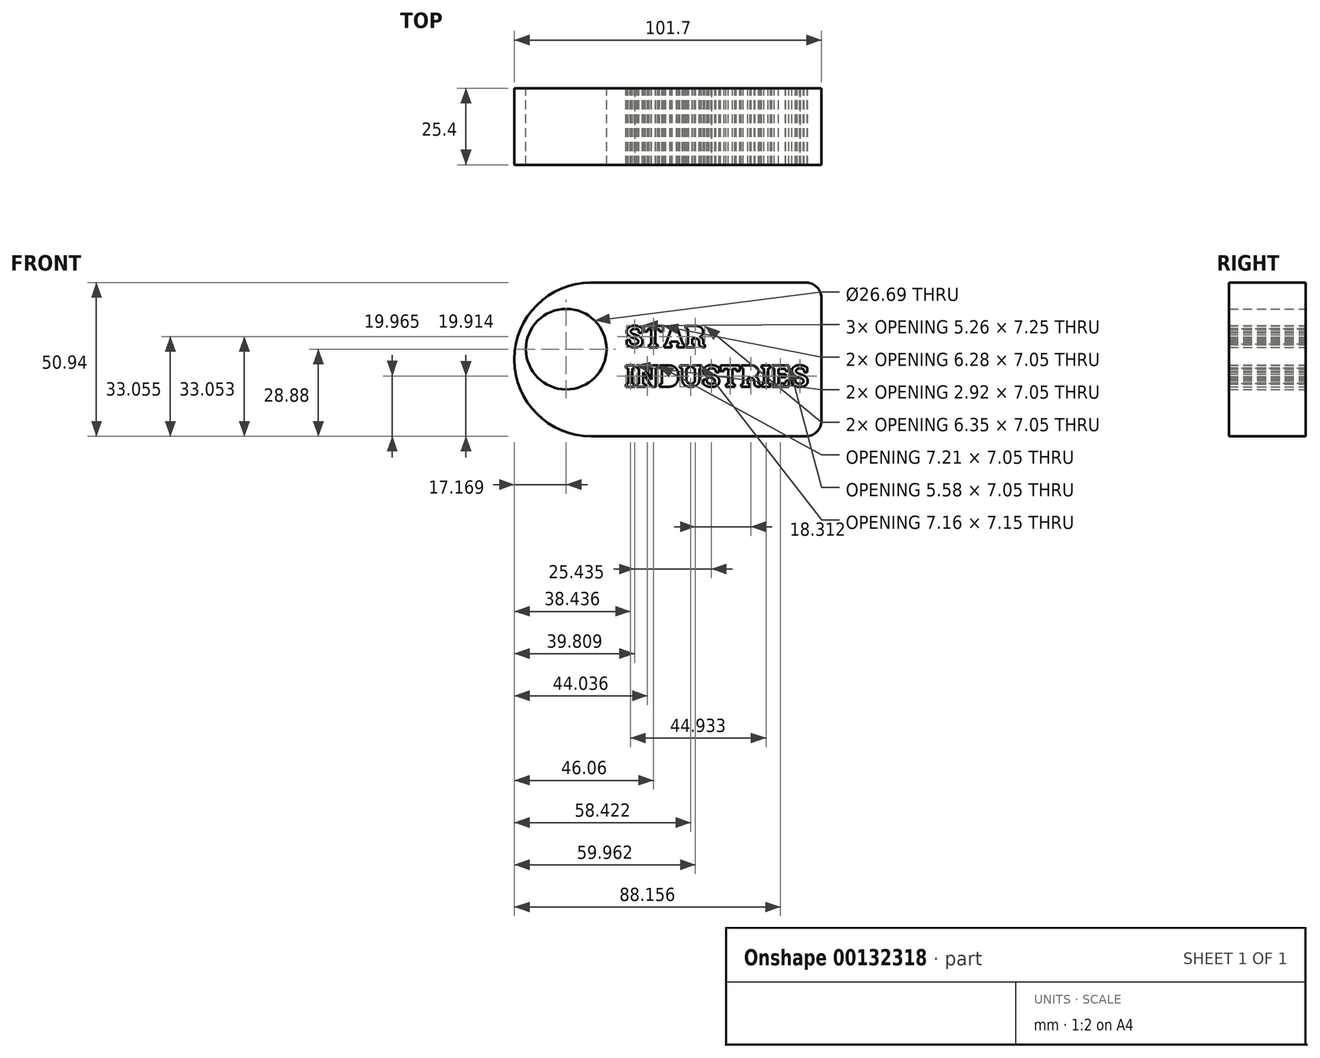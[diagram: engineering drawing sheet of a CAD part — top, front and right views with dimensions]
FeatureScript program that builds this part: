
annotation { "Feature Type Name" : "Feature", "Feature Type Description" : "" }
export const myFeature = defineFeature(function(context is Context, id is Id, definition is map)
    precondition{}
    {
        {
            var Q0;
            Q0=qCreatedBy(makeId("Front.planeOp"),FACE);
            var sketch = newSketch(context, id + "F0", { "sketchPlane" : qUnion([Q0])});
            skLineSegment(sketch, "E0.bottom", {"start": v(-44.67, 22.06) * mm, "end": v(57.03, 22.06) * mm});
            skLineSegment(sketch, "E0.top", {"start": v(-44.67, -28.88) * mm, "end": v(57.03, -28.88) * mm});
            skLineSegment(sketch, "E0.left", {"start": v(-44.67, 22.06) * mm, "end": v(-44.67, -28.88) * mm});
            skLineSegment(sketch, "E0.right", {"start": v(57.03, 22.06) * mm, "end": v(57.03, -28.88) * mm});
            skCircle(sketch, "E1", {"center": v(-27.5, 0) * mm, "radius": 13.35 * mm});
            skText(sketch, "E2", { "text": "STAR\nINDUSTRIES", "fontName": "RobotoSlab-Bold.ttf"});
            const initialGuessF0  = {"E2": [-0.00796, 0.00065, 1, 0, 0.00714]};
            skSetInitialGuess(sketch, initialGuessF0);
            skSolve(sketch);
        }
        {
            var Q0;
            Q0 = qSketchRegion(id + "F0", true);
            extrude(context, id + "F1", {"entities" : qUnion([Q0]), "depth" : 25.4 * mm});
        }
        {
            var Q0;
            Q0=makeQuery(id+"F1.opExtrude","SWEPT_EDGE",EDGE,{"disambiguationData":[OSD([sQuery(id+"F0.wireOp",EDGE,"E0.bottom"),sQuery(id+"F0.wireOp",EDGE,"E0.left")])]});
            var Q1;
            Q1=makeQuery(id+"F1.opExtrude","SWEPT_EDGE",EDGE,{"disambiguationData":[OSD([sQuery(id+"F0.wireOp",EDGE,"E0.top"),sQuery(id+"F0.wireOp",EDGE,"E0.left")])]});
            fillet(context, id + "F2", {"entities" : qUnion([Q0, Q1]), "radius" : 25.4 * mm, "tangentPropagation" : true, "allowEdgeOverflow" : false});
        }
        {
            var Q0;
            Q0=makeQuery(id+"F1.opExtrude","SWEPT_EDGE",EDGE,{"disambiguationData":[OSD([sQuery(id+"F0.wireOp",EDGE,"E0.bottom"),sQuery(id+"F0.wireOp",EDGE,"E0.right")])]});
            var Q1;
            Q1=makeQuery(id+"F1.opExtrude","SWEPT_EDGE",EDGE,{"disambiguationData":[OSD([sQuery(id+"F0.wireOp",EDGE,"E0.top"),sQuery(id+"F0.wireOp",EDGE,"E0.right")])]});
            fillet(context, id + "F3", {"entities" : qUnion([Q0, Q1]), "radius" : 5.08 * mm, "tangentPropagation" : true, "allowEdgeOverflow" : false});
        }
    });
